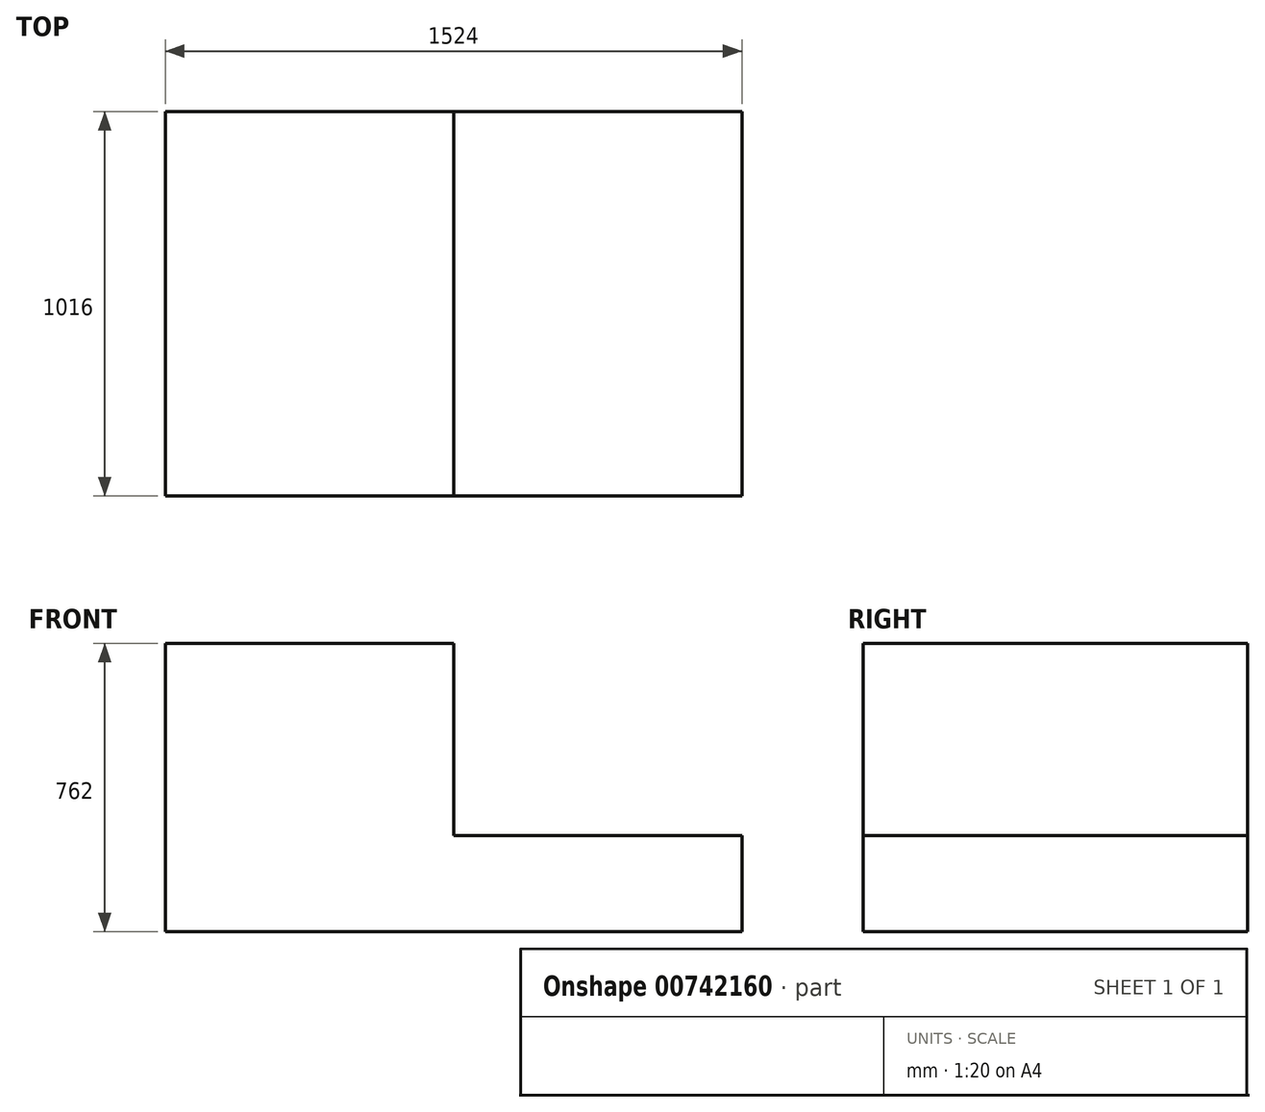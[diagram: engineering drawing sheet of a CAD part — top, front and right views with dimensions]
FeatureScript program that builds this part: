
annotation { "Feature Type Name" : "Feature", "Feature Type Description" : "" }
export const myFeature = defineFeature(function(context is Context, id is Id, definition is map)
    precondition{}
    {
        {
            var Q0;
            Q0=qCreatedBy(makeId("Front.planeOp"),FACE);
            var sketch = newSketch(context, id + "F0", { "sketchPlane" : qUnion([Q0])});
            skLineSegment(sketch, "E0", {"start": v(-762, 0) * mm, "end": v(762, 0) * mm});
            skLineSegment(sketch, "E1", {"start": v(762, 0) * mm, "end": v(762, 254) * mm});
            skLineSegment(sketch, "E2", {"start": v(762, 254) * mm, "end": v(0, 254) * mm});
            skLineSegment(sketch, "E3", {"start": v(-762, 0) * mm, "end": v(-762, 762) * mm});
            skLineSegment(sketch, "E4", {"start": v(-762, 762) * mm, "end": v(0, 762) * mm});
            skLineSegment(sketch, "E5", {"start": v(0, 762) * mm, "end": v(0, 254) * mm});
            skSolve(sketch);
        }
        {
            var Q0;
            Q0 = qSketchRegion(id + "F0", true);
            extrude(context, id + "F1", {"entities" : qUnion([Q0]), "depth" : 1016 * mm, "offsetDistance" : 25.4 * mm});
        }
    });
